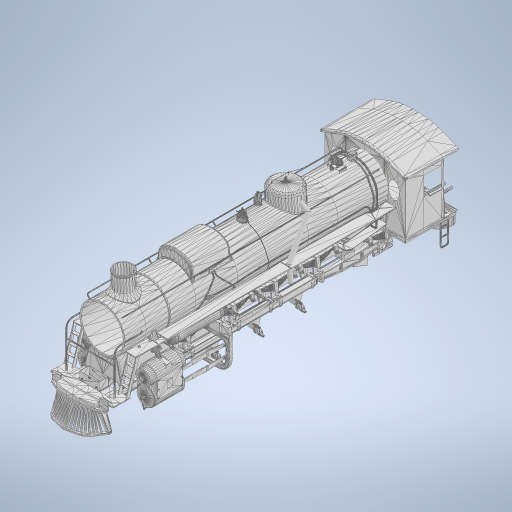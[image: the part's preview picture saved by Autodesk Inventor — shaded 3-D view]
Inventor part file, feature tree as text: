
AUTODESK INVENTOR PART (.ipt)
format: ipt  version: 2023 (Build 270158000, 158)  size: 1,691,648 bytes
history: native  units: in
note: dims shown in document units (in); Inventor stores cm internally (conversion verified against a paired STEP export)
features: other x2, sketch x2, plane x1, sweep x1
ambient origin geometry x8: Origin, YZ Plane, XZ Plane, XY Plane, X Axis, Y Axis, Z Axis, Center Point
bodies: Solid1 (feature_tree)
feature tree (6):
  other  "s282_locomotive_body"
  sketch  "3D Sketch1"
  plane  "Work Plane1"
  sweep  "Sweep1"
  sketch  "Sketch1"  dims[d0=0.0in d1=0.0in d2=6.0in]
  other  "s282_locomotive_body_0"
